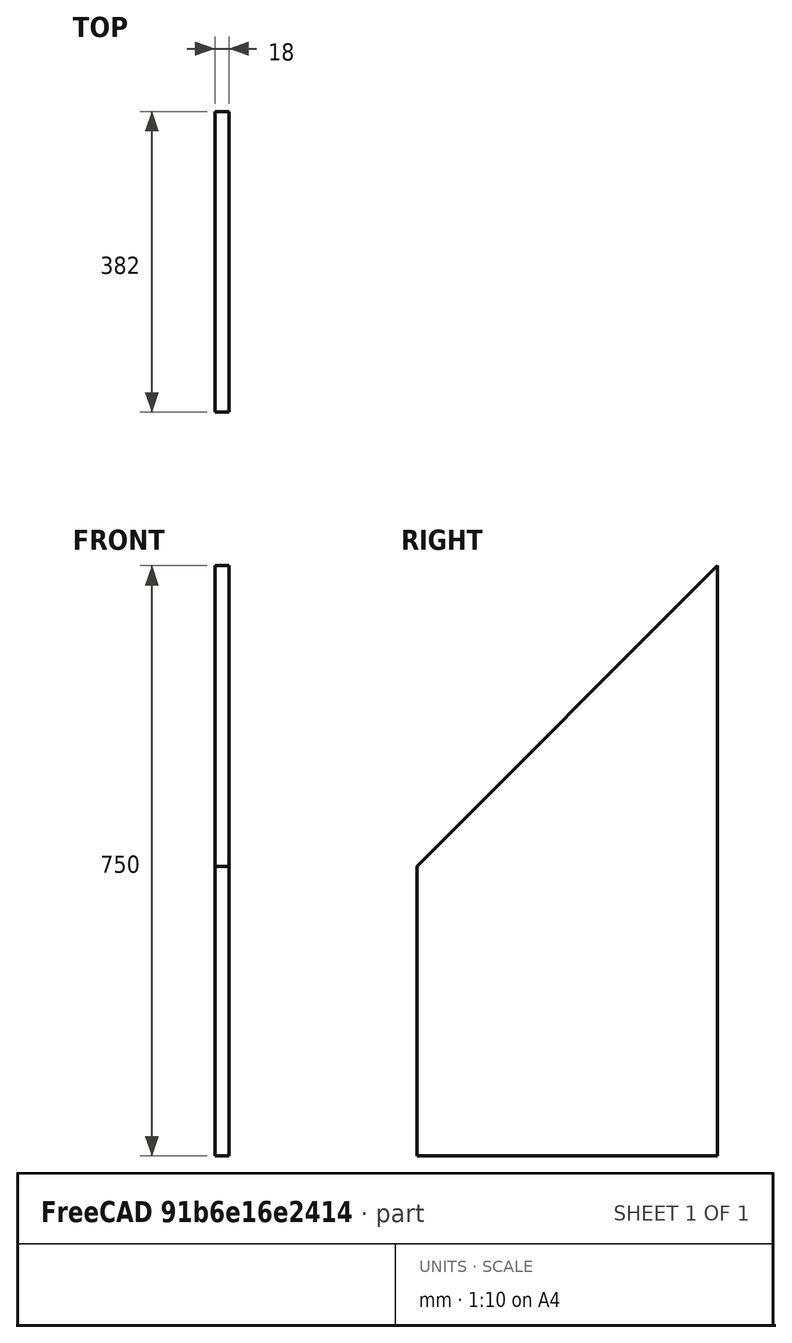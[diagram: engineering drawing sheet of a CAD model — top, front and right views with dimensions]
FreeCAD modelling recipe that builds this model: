
FCSTD DOCUMENT  (FreeCAD 0.18R4 (GitTag))
Label: right_side
License: All rights reserved
LicenseURL: http://en.wikipedia.org/wiki/All_rights_reserved
objects: Sketcher::SketchObject×1, PartDesign::Pad×1, PartDesign::Body×1
note: 4 computed .brp shape members not serialized (recipe doc carries the construction recipe); baked Part::Feature solids carry a one-line shape summary decoded from their .brp

FEATURE [Sketcher::SketchObject] Sketch
  MapMode = 5
  Placement = pos=(0,0,0) rot=(0.57735,0.57735,0.57735;2.0944rad)
  Support = -> [YZ_Plane]
  sketch-geometry (4):
    g0: LineSegment StartX=0 StartY=0 StartZ=0 EndX=-382 EndY=0 EndZ=0
    g1: LineSegment StartX=-382 StartY=0 StartZ=0 EndX=-382 EndY=368 EndZ=0
    g2: LineSegment StartX=-382 StartY=368 StartZ=0 EndX=0 EndY=750 EndZ=0
    g3: LineSegment StartX=0 StartY=750 StartZ=0 EndX=0 EndY=0 EndZ=0
  constraints (11):
    c: Coincident(g3,g0)
    c: Coincident(g0,g-1)
    c: Coincident(g0,g1)
    c: Coincident(g1,g2)
    c: Coincident(g2,g3)
    c: Vertical(g3)
    c: Vertical(g1)
    c: Horizontal(g0)
    c: DistanceX(g0,g0) = 382
    c: DistanceY(g3,g3) = 750
    c: Angle(g2,g3) = 0.785398
FEATURE [PartDesign::Pad] Pad
  Length = 18
  Length2 = 100
  Placement = pos=(0,0,0) rot=(0.57735,0.57735,0.57735;2.0944rad)
  Profile = -> Sketch
  Type = 0
FEATURE [PartDesign::Body] Body
  Group = -> [Sketch,Pad]
  Origin = -> Origin
  Tip = -> Pad
